# Revit family: JOMA_Balksko kombi_Grundform 380
name_source: partatom
category: Structural Connections
revit_build: Autodesk Revit Structure 2012 (Build: 20110309_2315(x64)
units: mm (PartAtom-declared; Revit-internal decimal feet)

## types (9) — shared parameters
D = 40 mm  [stored 0.131234 ft]
Default Elevation = 1219 mm
E = 42 mm  [stored 0.137795 ft]
F = 78 mm  [stored 0.255906 ft]
Grundform 380 = Yes
Länk Joma Dimensioneringsverktyg = http://www.joma.se
Material = Varmförzinkad stålplåt
Typ = GRUNDFORM 380
Vikt = 0,43
Y = 101 mm  [stored 0.331365 ft]

## per-type parameters (varying)
| type | A | B | X |
| 5245168  45x168 | 45 mm  [stored 0.147638 ft] | 168 mm  [stored 0.551181 ft] | 38 mm  [stored 0.124672 ft] |
| 5251164  51x164 | 51 mm | 164 mm  [stored 0.538058 ft] | 38 mm  [stored 0.124672 ft] |
| 5270155  70x155 | 70 mm  [stored 0.229659 ft] | 155 mm  [stored 0.50853 ft] | 38 mm  [stored 0.124672 ft] |
| 5280150  80x150 | 80 mm  [stored 0.262467 ft] | 150 mm | 38 mm  [stored 0.124672 ft] |
| 5290145  90x145 | 90 mm  [stored 0.295276 ft] | 145 mm  [stored 0.475722 ft] | 38 mm  [stored 0.124672 ft] |
| 5210140  100x140 | 100 mm  [stored 0.328084 ft] | 140 mm  [stored 0.459318 ft] | 37 mm  [stored 0.121391 ft] |
| 5260160  60x160 | 60 mm  [stored 0.19685 ft] | 160 mm  [stored 0.524934 ft] | 38 mm  [stored 0.124672 ft] |
| 5248166  48x166 | 48 mm  [stored 0.15748 ft] | 166 mm  [stored 0.544619 ft] | 38 mm  [stored 0.124672 ft] |
| 5276152  76x152 | 76 mm  [stored 0.249344 ft] | 152 mm  [stored 0.498688 ft] | 38 mm  [stored 0.124672 ft] |

note: [stored X ft] marks values corroborated as IEEE doubles in the binary element streams (Revit-internal decimal feet)

## geometry (parser evidence)
native form markers: Sweep x1
no freeform markers — native parametric forms only
